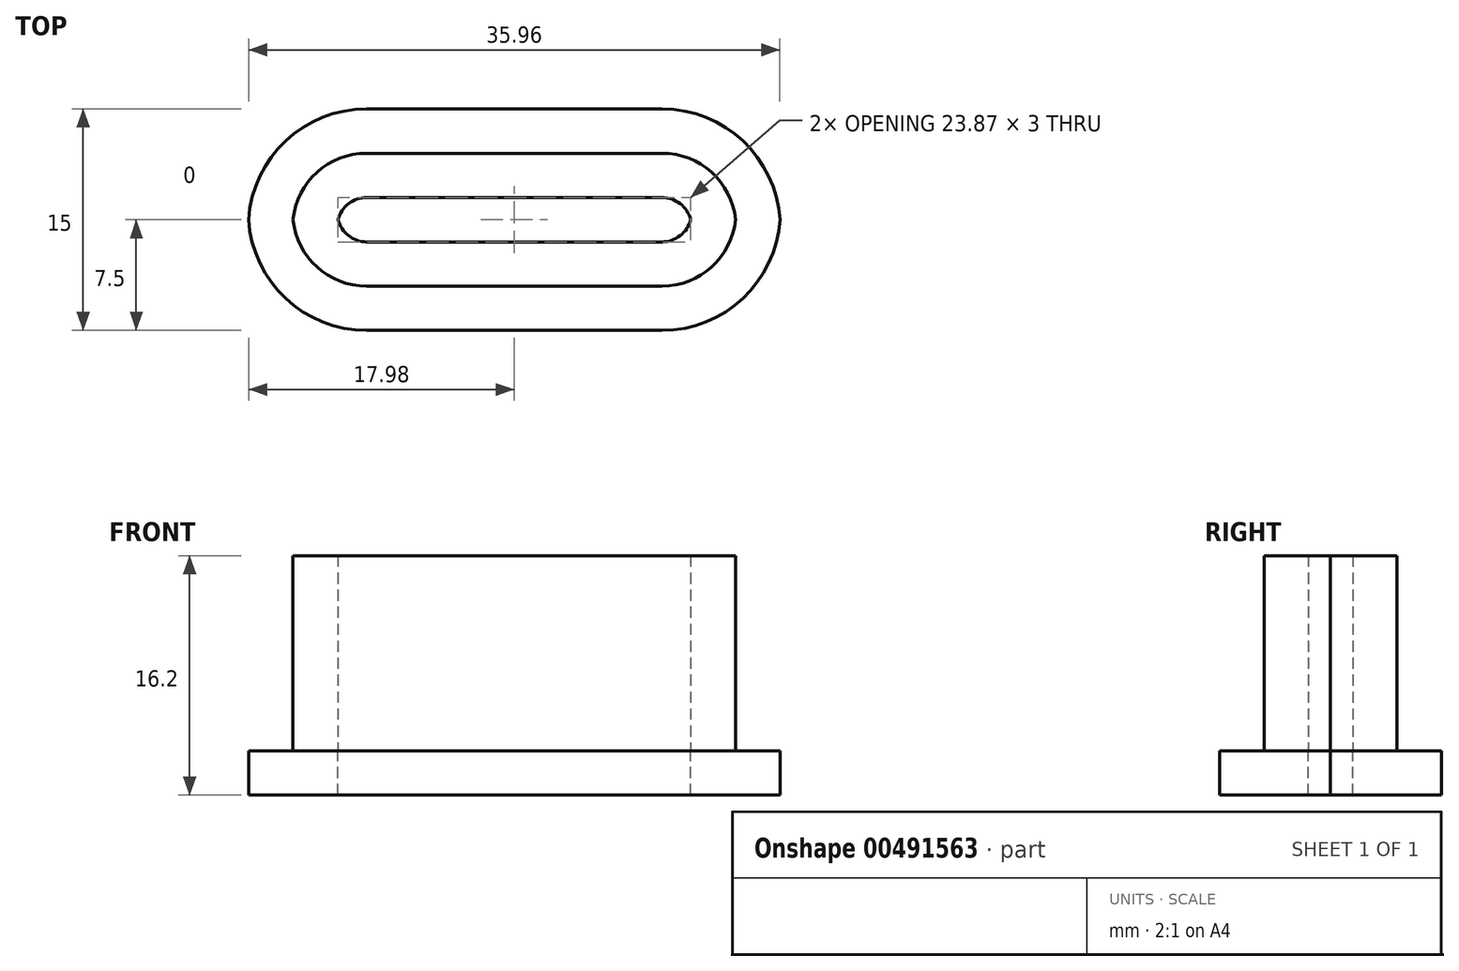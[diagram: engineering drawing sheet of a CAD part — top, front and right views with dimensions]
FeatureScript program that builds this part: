
annotation { "Feature Type Name" : "Feature", "Feature Type Description" : "" }
export const myFeature = defineFeature(function(context is Context, id is Id, definition is map)
    precondition{}
    {
        {
            assignVariable(context, id + "F0", {"name" : "wallThickness", "anyValue" : 3.2});
        }
        {
            assignVariable(context, id + "F1", {"name" : "lipDepth", "anyValue" : 3});
        }
        {
            assignVariable(context, id + "F2", {"name" : "innerLipProtrude", "anyValue" : 10});
        }
        {
            var Q0;
            Q0=qCreatedBy(makeId("Top.planeOp"),FACE);
            var sketch = newSketch(context, id + "F3", { "sketchPlane" : qUnion([Q0])});
            skLineSegment(sketch, "E0.top", {"start": v(0, 2) * mm, "end": v(-10, 2) * mm});
            skLineSegment(sketch, "E0.left", {"start": v(0, 0) * mm, "end": v(0, 2) * mm, "construction": true});
            skArc(sketch, "E1", {"start": v(-10, 2) * mm, "mid": v(-11.22, 1.58) * mm, "end": v(-11.94, 0.5) * mm});
            skLineSegment(sketch, "E2.MirrorCS", {"start": v(0, 2) * mm, "end": v(10, 2) * mm});
            skArc(sketch, "E3.MirrorCS", {"start": v(10, 2) * mm, "mid": v(11.22, 1.58) * mm, "end": v(11.94, 0.5) * mm});
            skLineSegment(sketch, "E4", {"start": v(-11.94, 0.5) * mm, "end": v(11.94, 0.5) * mm, "construction": true});
            skArc(sketch, "E5.MirrorCS", {"start": v(-10, -1) * mm, "mid": v(-11.22, -0.58) * mm, "end": v(-11.94, 0.5) * mm});
            skLineSegment(sketch, "E6.MirrorCS", {"start": v(0, -1) * mm, "end": v(-10, -1) * mm});
            skLineSegment(sketch, "E7.MirrorCS", {"start": v(0, -1) * mm, "end": v(10, -1) * mm});
            skArc(sketch, "E8.MirrorCS", {"start": v(10, -1) * mm, "mid": v(11.22, -0.58) * mm, "end": v(11.94, 0.5) * mm});
            skLineSegment(sketch, "E9.0", {"start": v(0, -4) * mm, "end": v(10, -4) * mm});
            skArc(sketch, "E9.1", {"start": v(10, -4) * mm, "mid": v(13.35, -2.7) * mm, "end": v(14.97, 0.5) * mm});
            skLineSegment(sketch, "E9.2", {"start": v(0, -4) * mm, "end": v(-10, -4) * mm});
            skArc(sketch, "E9.3", {"start": v(10, 5) * mm, "mid": v(13.35, 3.7) * mm, "end": v(14.97, 0.5) * mm});
            skArc(sketch, "E9.4", {"start": v(-10, -4) * mm, "mid": v(-13.35, -2.7) * mm, "end": v(-14.97, 0.5) * mm});
            skArc(sketch, "E9.5", {"start": v(-10, 5) * mm, "mid": v(-13.35, 3.7) * mm, "end": v(-14.97, 0.5) * mm});
            skLineSegment(sketch, "E9.6", {"start": v(0, 5) * mm, "end": v(-10, 5) * mm});
            skLineSegment(sketch, "E9.7", {"start": v(0, 5) * mm, "end": v(10, 5) * mm});
            skLineSegment(sketch, "E10.0", {"start": v(0, -7) * mm, "end": v(-10, -7) * mm});
            skArc(sketch, "E10.1", {"start": v(-10, -7) * mm, "mid": v(-15.48, -4.83) * mm, "end": v(-17.98, 0.5) * mm});
            skLineSegment(sketch, "E10.2", {"start": v(0, -7) * mm, "end": v(10, -7) * mm});
            skArc(sketch, "E10.3", {"start": v(-10, 8) * mm, "mid": v(-15.48, 5.83) * mm, "end": v(-17.98, 0.5) * mm});
            skArc(sketch, "E10.4", {"start": v(10, -7) * mm, "mid": v(15.48, -4.83) * mm, "end": v(17.98, 0.5) * mm});
            skArc(sketch, "E10.5", {"start": v(10, 8) * mm, "mid": v(15.48, 5.83) * mm, "end": v(17.98, 0.5) * mm});
            skLineSegment(sketch, "E10.6", {"start": v(0, 8) * mm, "end": v(10, 8) * mm});
            skLineSegment(sketch, "E10.7", {"start": v(0, 8) * mm, "end": v(-10, 8) * mm});
            skSolve(sketch);
        }
        {
            var Q0;
            Q0=makeQuery(id+"F3.imprint","IMPRINT",FACE,{"disambiguationData":[TD([[makeQuery(id+"F3.imprint","IMPRINT",EDGE,{"derivedFrom":sQuery(id+"F3.wireOp",EDGE,"E9.0")}),-1.0]])]});
            var Q1;
            Q1=makeQuery(id+"F3.imprint","IMPRINT",FACE,{"disambiguationData":[TD([[makeQuery(id+"F3.imprint","IMPRINT",EDGE,{"derivedFrom":sQuery(id+"F3.wireOp",EDGE,"E0.top")}),-1.0]])]});
            extrude(context, id + "F4", {"entities" : qUnion([Q0, Q1]), "oppositeDirection" : true, "depth" : (getVariable(context, 'lipDepth')) * mm, "offsetDistance" : 25 * mm});
        }
        {
            var Q0;
            Q0=makeQuery(id+"F3.imprint","IMPRINT",FACE,{"disambiguationData":[TD([[makeQuery(id+"F3.imprint","IMPRINT",EDGE,{"derivedFrom":sQuery(id+"F3.wireOp",EDGE,"E0.top")}),-1.0]])]});
            extrude(context, id + "F5", {"entities" : qUnion([Q0]), "depth" : (getVariable(context, 'wallThickness') + getVariable(context, 'innerLipProtrude')) * mm, "offsetDistance" : 25 * mm});
        }
    });
